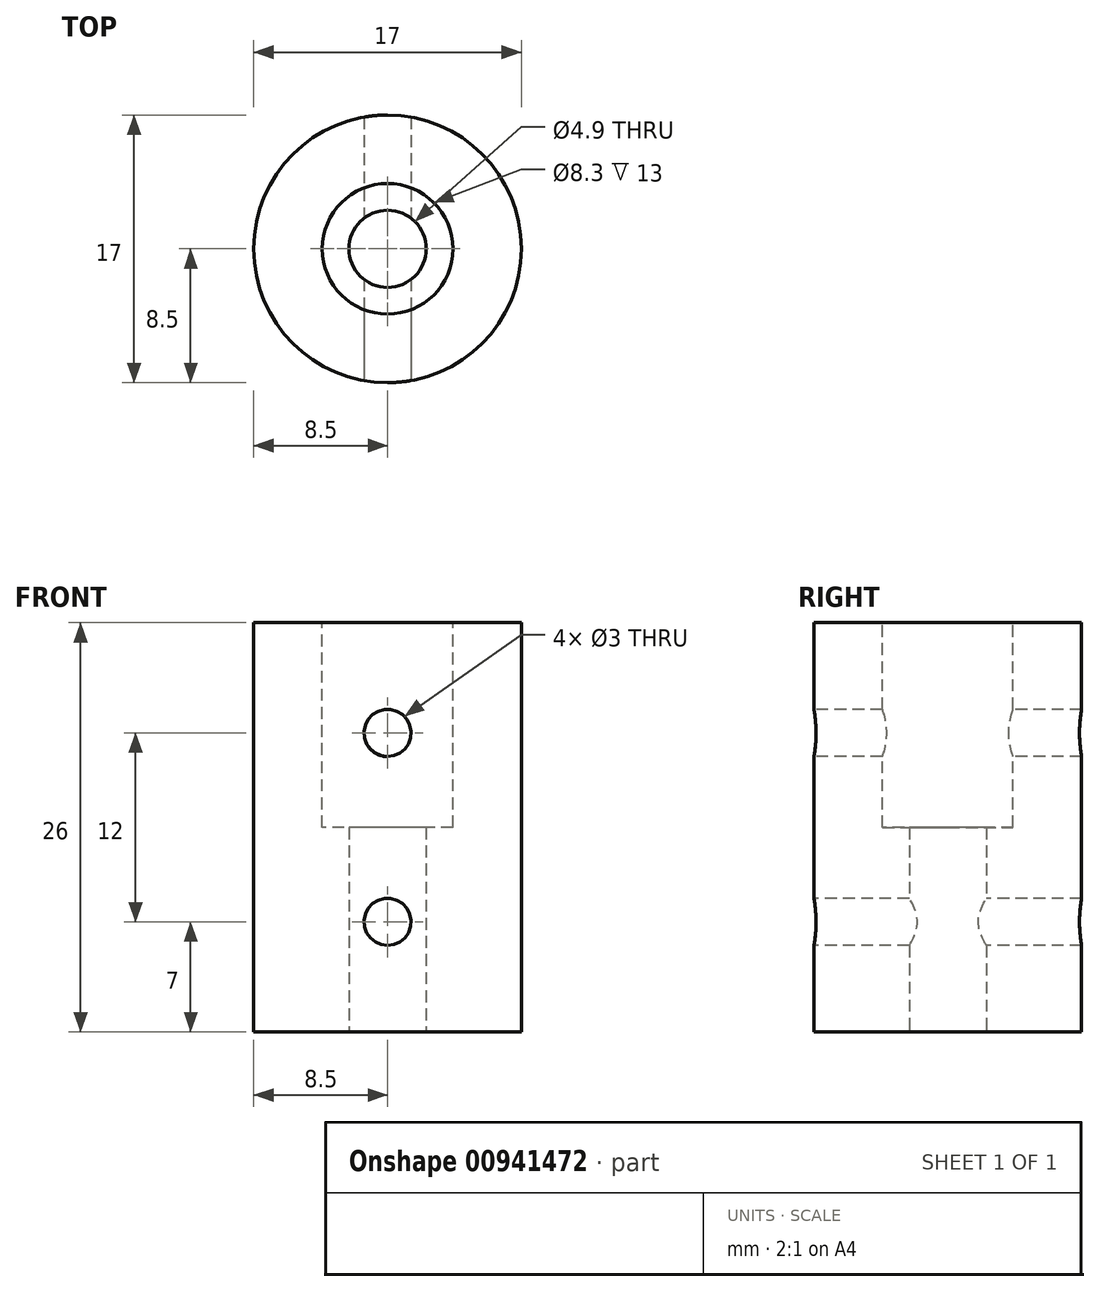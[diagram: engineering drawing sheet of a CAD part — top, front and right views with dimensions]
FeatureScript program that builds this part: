
annotation { "Feature Type Name" : "Feature", "Feature Type Description" : "" }
export const myFeature = defineFeature(function(context is Context, id is Id, definition is map)
    precondition{}
    {
        {
            var Q0;
            Q0=qCreatedBy(makeId("Top.planeOp"),FACE);
            var sketch = newSketch(context, id + "F0", { "sketchPlane" : qUnion([Q0])});
            skCircle(sketch, "E0", {"center": v(0, 0) * mm, "radius": 2.45 * mm});
            skCircle(sketch, "E1", {"center": v(0, 0) * mm, "radius": 8.5 * mm});
            skSolve(sketch);
        }
        {
            var Q0;
            Q0=makeQuery(id+"F0.imprint","IMPRINT",FACE,{"disambiguationData":[TD([[makeQuery(id+"F0.imprint","IMPRINT",EDGE,{"derivedFrom":sQuery(id+"F0.wireOp",EDGE,"E0")}),-1.0]])]});
            extrude(context, id + "F1", {"entities" : qUnion([Q0]), "depth" : 26 * mm, "offsetDistance" : 25 * mm});
        }
        {
            var Q0;
            Q0=makeQuery(id+"F1.opExtrude","CAP_FACE",FACE,{"disambiguationData":[OSD([sQuery(id+"F0.wireOp",EDGE,"E0"),sQuery(id+"F0.wireOp",EDGE,"E1")])],"isStart":false});
            var sketch = newSketch(context, id + "F2", { "sketchPlane" : qUnion([Q0])});
            skCircle(sketch, "E2", {"center": v(0, 0) * mm, "radius": 4.15 * mm});
            skSolve(sketch);
        }
        {
            var Q0;
            Q0=makeQuery(id+"F2.imprint","IMPRINT",FACE,{"disambiguationData":[TD([[makeQuery(id+"F2.imprint","IMPRINT",EDGE,{"derivedFrom":sQuery(id+"F2.wireOp",EDGE,"E2")}),1.0]])]});
            extrude(context, id + "F3", {"entities" : qUnion([Q0]), "operationType" : NewBodyOperationType.REMOVE, "oppositeDirection" : true, "depth" : 13 * mm, "offsetDistance" : 25 * mm});
        }
        {
            var Q0;
            Q0=qCreatedBy(makeId("Front.planeOp"),FACE);
            var sketch = newSketch(context, id + "F4", { "sketchPlane" : qUnion([Q0])});
            skCircle(sketch, "E3", {"center": v(0, 19) * mm, "radius": 1.5 * mm});
            skCircle(sketch, "E4", {"center": v(0, 7) * mm, "radius": 1.5 * mm});
            skSolve(sketch);
        }
        {
            var Q0;
            Q0 = qSketchRegion(id + "F4", true);
            extrude(context, id + "F5", {"entities" : qUnion([Q0]), "operationType" : NewBodyOperationType.REMOVE, "oppositeDirection" : true, "depth" : 25 * mm, "offsetDistance" : 25 * mm, "hasSecondDirection" : true, "secondDirectionOppositeDirection" : false, "secondDirectionDepth" : 25 * mm});
        }
    });
